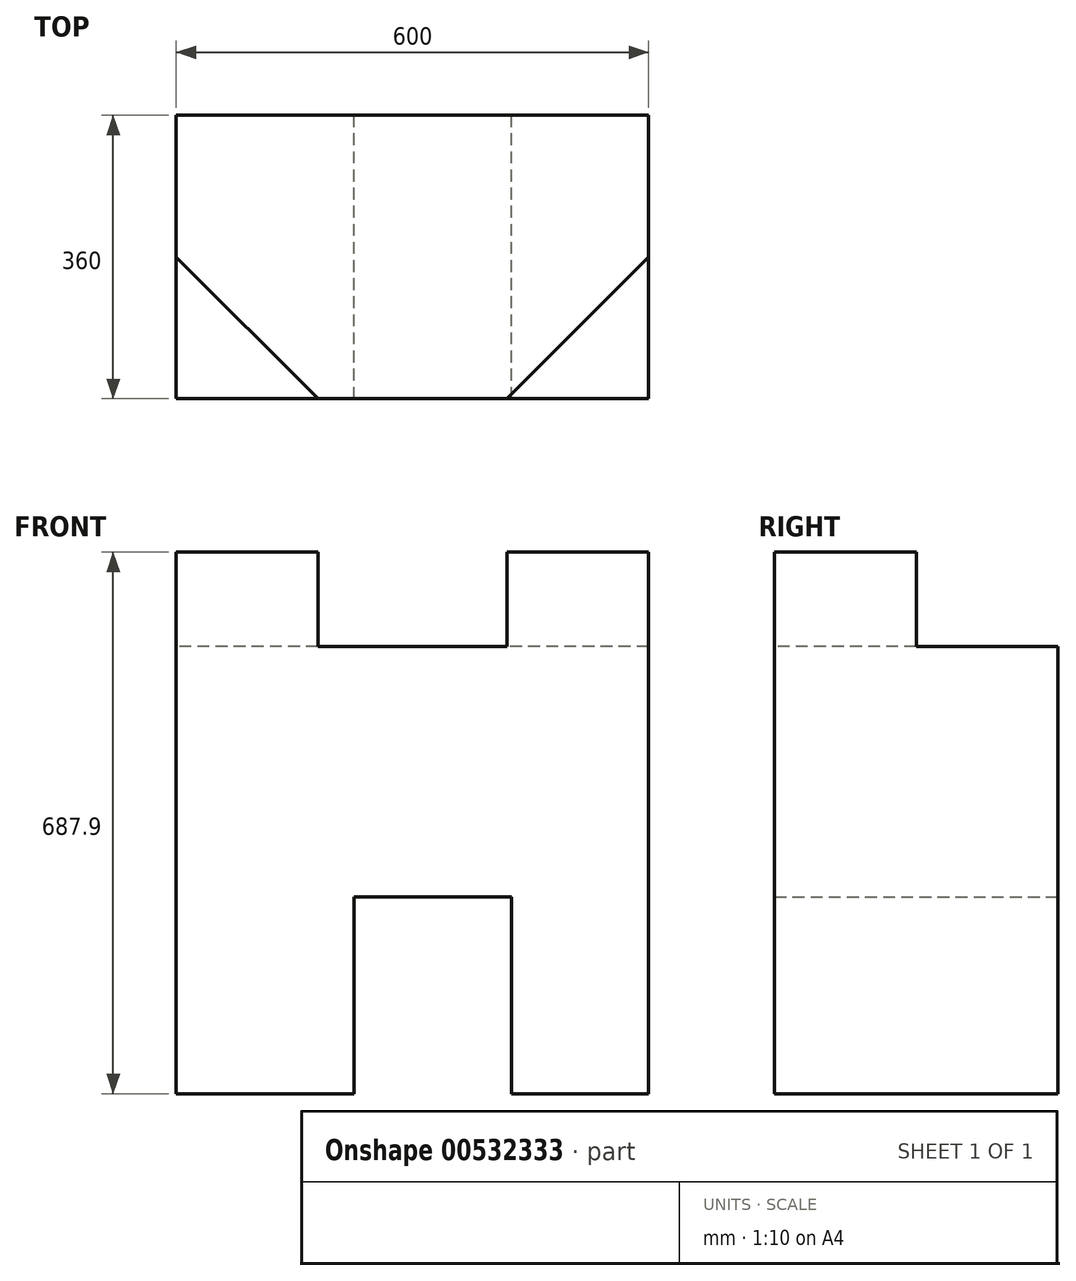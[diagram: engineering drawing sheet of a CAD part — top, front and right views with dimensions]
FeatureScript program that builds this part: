
annotation { "Feature Type Name" : "Feature", "Feature Type Description" : "" }
export const myFeature = defineFeature(function(context is Context, id is Id, definition is map)
    precondition{}
    {
        {
            var Q0;
            Q0=qCreatedBy(makeId("Front.planeOp"),FACE);
            var sketch = newSketch(context, id + "F0", { "sketchPlane" : qUnion([Q0])});
            skLineSegment(sketch, "E0.bottom", {"start": v(-300, -283.95) * mm, "end": v(-73.95, -283.95) * mm});
            skLineSegment(sketch, "E0.top", {"start": v(-300, 283.95) * mm, "end": v(300, 283.95) * mm});
            skLineSegment(sketch, "E0.left", {"start": v(-300, -283.95) * mm, "end": v(-300, 283.95) * mm});
            skLineSegment(sketch, "E0.right", {"start": v(300, -283.95) * mm, "end": v(300, 283.95) * mm});
            skPoint(sketch, "E0.middle", {"position": v(0, 0) * mm});
            skLineSegment(sketch, "E1", {"start": v(-73.95, -283.95) * mm, "end": v(-73.95, -33.95) * mm});
            skLineSegment(sketch, "E2", {"start": v(-73.95, -33.95) * mm, "end": v(126.05, -33.95) * mm});
            skLineSegment(sketch, "E3", {"start": v(126.05, -33.95) * mm, "end": v(126.05, -283.95) * mm});
            skLineSegment(sketch, "E4", {"start": v(126.05, -283.95) * mm, "end": v(300, -283.95) * mm});
            skSolve(sketch);
        }
        {
            var Q0;
            Q0 = qSketchRegion(id + "F0", true);
            extrude(context, id + "F1", {"entities" : qUnion([Q0]), "depth" : 360 * mm, "offsetDistance" : 25.4 * mm});
        }
        {
            var Q0;
            Q0=makeQuery(id+"F1.opExtrude","SWEPT_FACE",FACE,{"disambiguationData":[OSD([sQuery(id+"F0.wireOp",EDGE,"E0.top")])]});
            var sketch = newSketch(context, id + "F2", { "sketchPlane" : qUnion([Q0])});
            skLineSegment(sketch, "E5", {"start": v(-300, -360) * mm, "end": v(-120, -360) * mm});
            skLineSegment(sketch, "E6", {"start": v(-120, -360) * mm, "end": v(-300, -180) * mm});
            skLineSegment(sketch, "E7", {"start": v(-300, -180) * mm, "end": v(-300, -360) * mm});
            skLineSegment(sketch, "E8", {"start": v(300, -360) * mm, "end": v(300, -180) * mm});
            skLineSegment(sketch, "E9", {"start": v(300, -180) * mm, "end": v(120, -360) * mm});
            skLineSegment(sketch, "E10", {"start": v(120, -360) * mm, "end": v(300, -360) * mm});
            skSolve(sketch);
        }
        {
            var Q0;
            Q0=makeQuery(id+"F2.imprint","IMPRINT",FACE,{"disambiguationData":[TD([[makeQuery(id+"F2.imprint","IMPRINT",EDGE,{"derivedFrom":sQuery(id+"F2.wireOp",EDGE,"E5")}),1.0]])]});
            var Q1;
            Q1=makeQuery(id+"F2.imprint","IMPRINT",FACE,{"disambiguationData":[TD([[makeQuery(id+"F2.imprint","IMPRINT",EDGE,{"derivedFrom":sQuery(id+"F2.wireOp",EDGE,"E8")}),1.0]])]});
            extrude(context, id + "F3", {"entities" : qUnion([Q0, Q1]), "operationType" : NewBodyOperationType.ADD, "depth" : 120 * mm, "offsetDistance" : 25.4 * mm});
        }
    });
